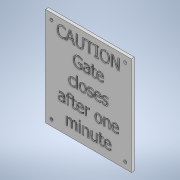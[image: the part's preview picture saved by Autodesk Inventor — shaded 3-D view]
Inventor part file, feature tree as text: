
AUTODESK INVENTOR PART (.ipt)
format: ipt  version: 2021.2 (Build 252289000, 289)  size: 1,028,096 bytes
history: native  units: in
note: dims shown in document units (in); Inventor stores cm internally (conversion verified against a paired STEP export)
features: sketch x3, extrude x1, emboss x1, hole x1
ambient origin geometry x8: Origin, YZ Plane, XZ Plane, XY Plane, X Axis, Y Axis, Z Axis, Center Point
bodies: Body1 (feature_tree)
feature tree (6):
  extrude  "Extrusion2"  Depth=7.0in
  emboss  "Emboss2"
  hole  "Hole1"  [1 undecoded]
  sketch  "Sketch4"  dims[d12=8.0in d13=7.0in]
  sketch  "Sketch5"  dims[d14=0.25in d15=0.0in d16=1.35in]
  sketch  "Sketch6"  dims[d17=0.1in d18=0.0in d19=7.0in d20=6.0in d21=0.25in d22=0.276in d23=0.507in d24=0.25in d25=0.5635in d26=1.0in d27=0.8108in]
note: 1 required parameter value undecoded (feature->parameter linkage not recoverable at this tier; creation-order binding heuristic only, values carry confidence <= 0.55)
